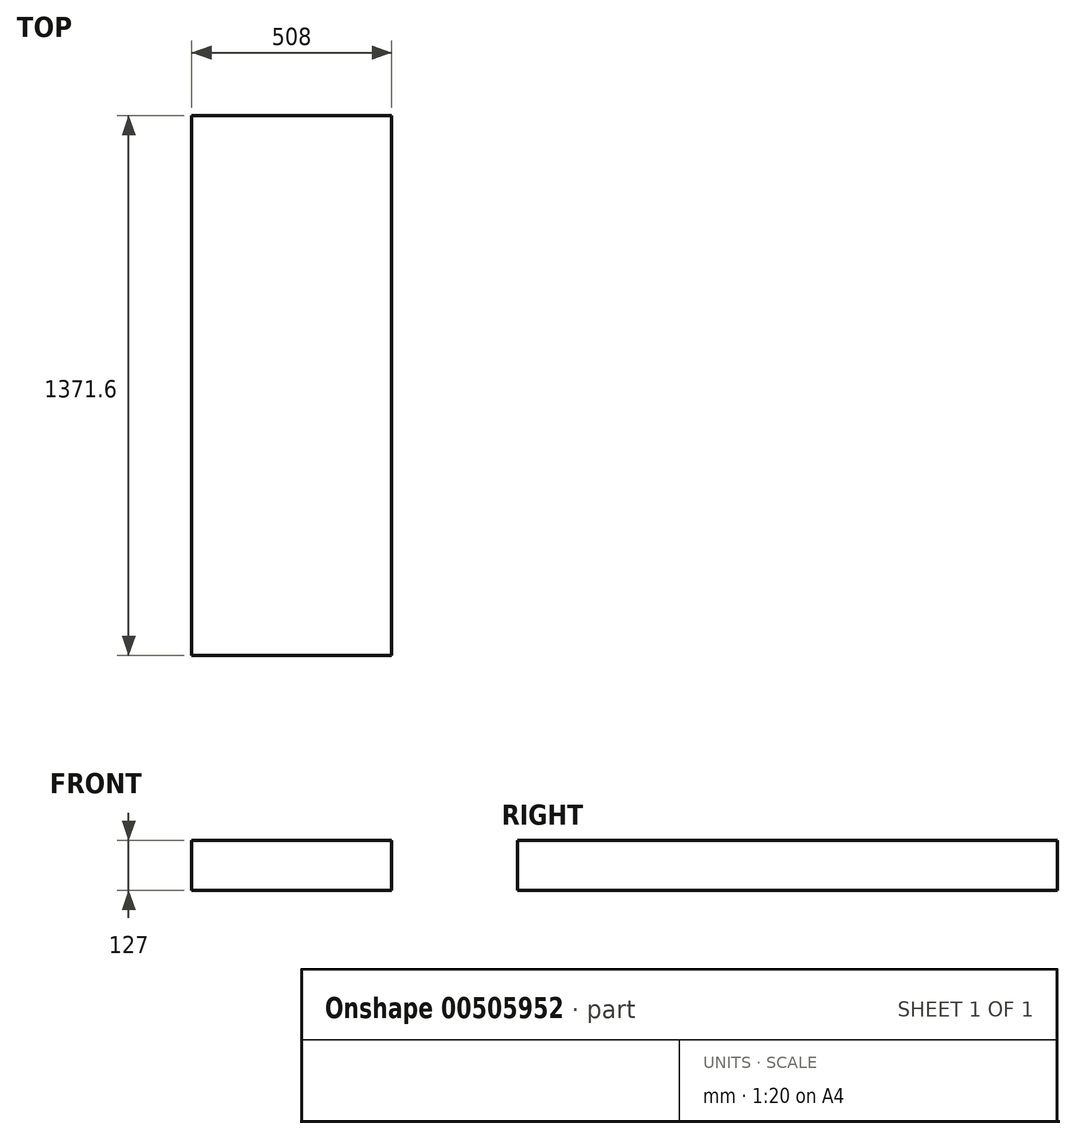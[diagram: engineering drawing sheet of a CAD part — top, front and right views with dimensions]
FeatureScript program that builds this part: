
annotation { "Feature Type Name" : "Feature", "Feature Type Description" : "" }
export const myFeature = defineFeature(function(context is Context, id is Id, definition is map)
    precondition{}
    {
        {
            var Q0;
            Q0=qCreatedBy(makeId("Top.planeOp"),FACE);
            var sketch = newSketch(context, id + "F0", { "sketchPlane" : qUnion([Q0])});
            skLineSegment(sketch, "E0.bottom", {"start": v(-447.44, 1330.15) * mm, "end": v(60.56, 1330.15) * mm});
            skLineSegment(sketch, "E0.top", {"start": v(-447.44, -41.45) * mm, "end": v(60.56, -41.45) * mm});
            skLineSegment(sketch, "E0.left", {"start": v(-447.44, 1330.15) * mm, "end": v(-447.44, -41.45) * mm});
            skLineSegment(sketch, "E0.right", {"start": v(60.56, 1330.15) * mm, "end": v(60.56, -41.45) * mm});
            skSolve(sketch);
        }
        {
            var Q0;
            Q0=makeQuery(id+"F0.imprint","IMPRINT",FACE,{"disambiguationData":[TD([[makeQuery(id+"F0.imprint","IMPRINT",EDGE,{"derivedFrom":sQuery(id+"F0.wireOp",EDGE,"E0.bottom")}),-1.0]])]});
            extrude(context, id + "F1", {"entities" : qUnion([Q0]), "depth" : 127 * mm, "offsetDistance" : 25.4 * mm});
        }
    });
